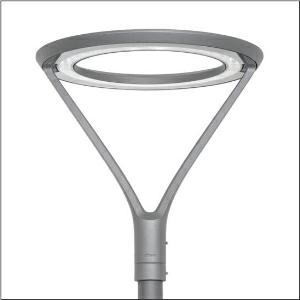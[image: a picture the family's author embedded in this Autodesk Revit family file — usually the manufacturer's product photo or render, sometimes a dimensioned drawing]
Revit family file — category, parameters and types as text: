
# Revit family: dl_r__20___st1_2a_5xa51283na008_e76f
name_source: partatom
category: Lighting Fixtures
units: mm (PartAtom-declared; Revit-internal decimal feet)

## family parameters
Cut with Voids When Loaded = No
Host = Face
Light Source = No
Part Type = Normal
Room Calculation Point = No
Round Connector Dimension = Use Diameter
Shared = No

## types (1)
- --- (1 x LED, 3030 lm, 23.2 W, 4000K)
    Apparent Load = 23 VA
    CIE Flux Codes = 32 72 97 100 100
    Color Rendering = 70
    Color Temperature = 4000K
    Default Elevation = 1800 mm
    Description = DL® 20, mast luminaire, primary light control with reflector, highly specular, primary optical cover: cover, of toughened safety glass of clear glass with excellent transmission level, light distribution: ST1.2a, light emission: direct distribution, primary light characteristic: asymmetric, installation type: post-top, LED, High Power LED, rated luminous flux: 3.010lm, luminous efficacy: 111lm/W, light colour: 740, colour temperature: 4000K, control gear: ECG Plus, control: overheat protection, power reduction, digital communication interface, constant luminous flux control, time-dependent luminous flux control, flexible luminous flux parameterisation, electronic power reduction, mains connection: 230..240V, 50/60Hz, connection cable pre-assembled, cable length: 5m, start of lifetime: 27W, end of service life: 28W, reduction: 14W, luminaire housing, upper part, of cast aluminium, powder-coated, Siteco® metallic grey (DB 702S), diameter: 690mm, height: 690mm, spigot size: 76mm (post-top), luminaire housing, of cast aluminium, powder-coated, Siteco® metallic grey (DB 702S), equipment: standard, protection rating (complete): IP66, insulation class (complete): insulation class II (safety insulation), certification: CE, ENEC, VDE, impact resistance: IK08, permissible operating ambient temperature: -25..+35°C, standard-compliant lighting for roads and squares, packaging unit: 1 piece

Light Distribution: ST1.2a
    Height = 690 mm
    Lamp = 1 x LED
    Lamp Light Flux = 3030 lm
    Lamp Power = 23.2 W
    Lamp count = 1
    Length = 690 mm
    Luminous efficacy = 131 lm/W
    Manufacturer = Siteco
    ModVariant = No
    Model = 5XA51283NA008
    Number of Poles = 1
    OnlyDefault = Yes
    Power Factor = 1
    Product Name = DL® 20 | ST1.2a
    Product group = mast luminaire | pylon top
    ProductGroupID = 6100
    Protection Class = Protection class II
    Protection Degree = IP 66
    RLX_Detail_Level = 1
    RLX_Emergency_Light_Flux = 0 lm
    RLX_Emergency_Type = 0
    RLX_Emergency_Type_DB = No
    RlxData = <blob elided: 207041 chars, md5=7b7babe6>
    Socket = socket
    Standby Power = 0 W
    System Light Flux = 3030 lm
    System Power = 23 W
    Type Comments = factory setting: luminous flux: 100 % | dim-lin: 254 | 310 mA
    Type Image = l_1006001.jpg
    URL = http://relux.com
    VarID = @adj_045725
    Voltage = 0 V
    Weight = 0.00 kg
    Width = 0 mm  [stored 0 ft]

note: [stored X ft] marks values corroborated as IEEE doubles in the binary element streams (Revit-internal decimal feet)

## geometry (parser evidence)
native form markers: Blend x4, Sweep x11
no freeform markers — native parametric forms only
